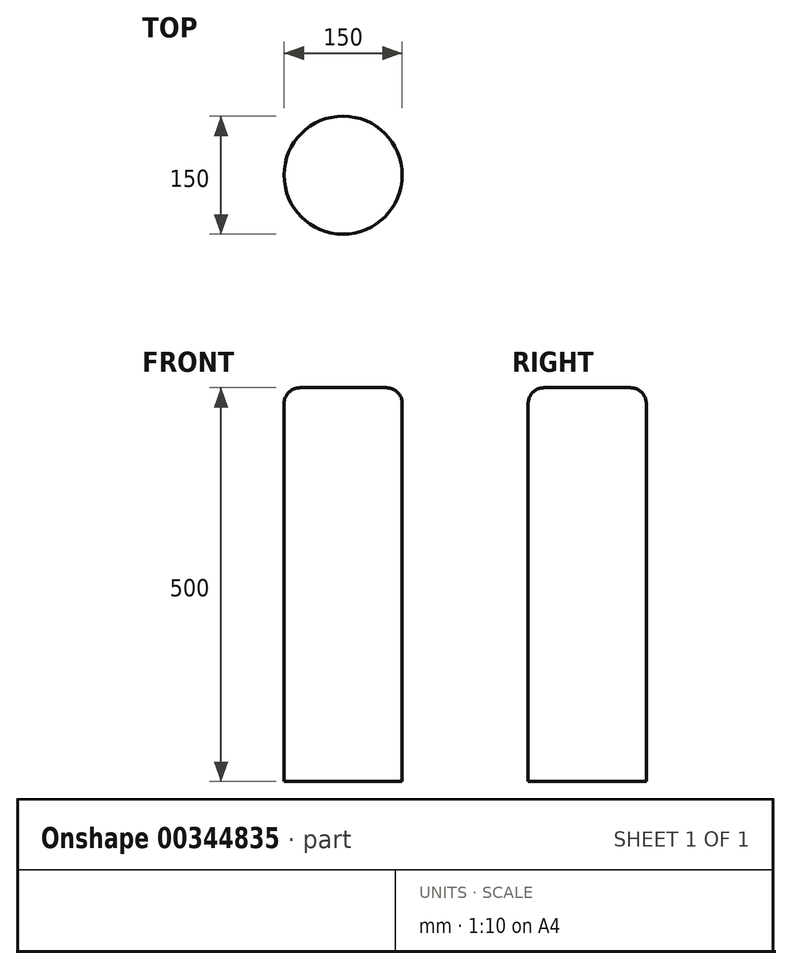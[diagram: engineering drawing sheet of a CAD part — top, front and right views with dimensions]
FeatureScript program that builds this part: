
annotation { "Feature Type Name" : "Feature", "Feature Type Description" : "" }
export const myFeature = defineFeature(function(context is Context, id is Id, definition is map)
    precondition{}
    {
        {
            var Q0;
            Q0=qCreatedBy(makeId("Front.planeOp"),FACE);
            var sketch = newSketch(context, id + "F0", { "sketchPlane" : qUnion([Q0])});
            skLineSegment(sketch, "E0", {"start": v(0, 420.85) * mm, "end": v(55, 420.85) * mm});
            skLineSegment(sketch, "E1", {"start": v(75, 400.85) * mm, "end": v(75, -79.15) * mm});
            skLineSegment(sketch, "E2", {"start": v(75, -79.15) * mm, "end": v(0, -79.15) * mm});
            skLineSegment(sketch, "E3", {"start": v(0, -79.15) * mm, "end": v(0, 420.85) * mm});
            skPoint(sketch, "E4.visualSharp", {"position": v(75, 420.85) * mm});
            skArc(sketch, "E4.filletArc", {"start": v(75, 400.85) * mm, "mid": v(69.14, 414.99) * mm, "end": v(55, 420.85) * mm});
            skSolve(sketch);
        }
        {
            var Q0;
            Q0=makeQuery(id+"F0.imprint","IMPRINT",FACE,{"disambiguationData":[TD([[makeQuery(id+"F0.imprint","IMPRINT",EDGE,{"derivedFrom":sQuery(id+"F0.wireOp",EDGE,"E0")}),-1.0]])]});
            var Q1;
            Q1=sQuery(id+"F0.wireOp",EDGE,"E3");
            revolve(context, id + "F1", {"entities" : qUnion([Q0]), "axis" : qUnion([Q1]), "revolveType" : RevolveType.FULL});
        }
    });
